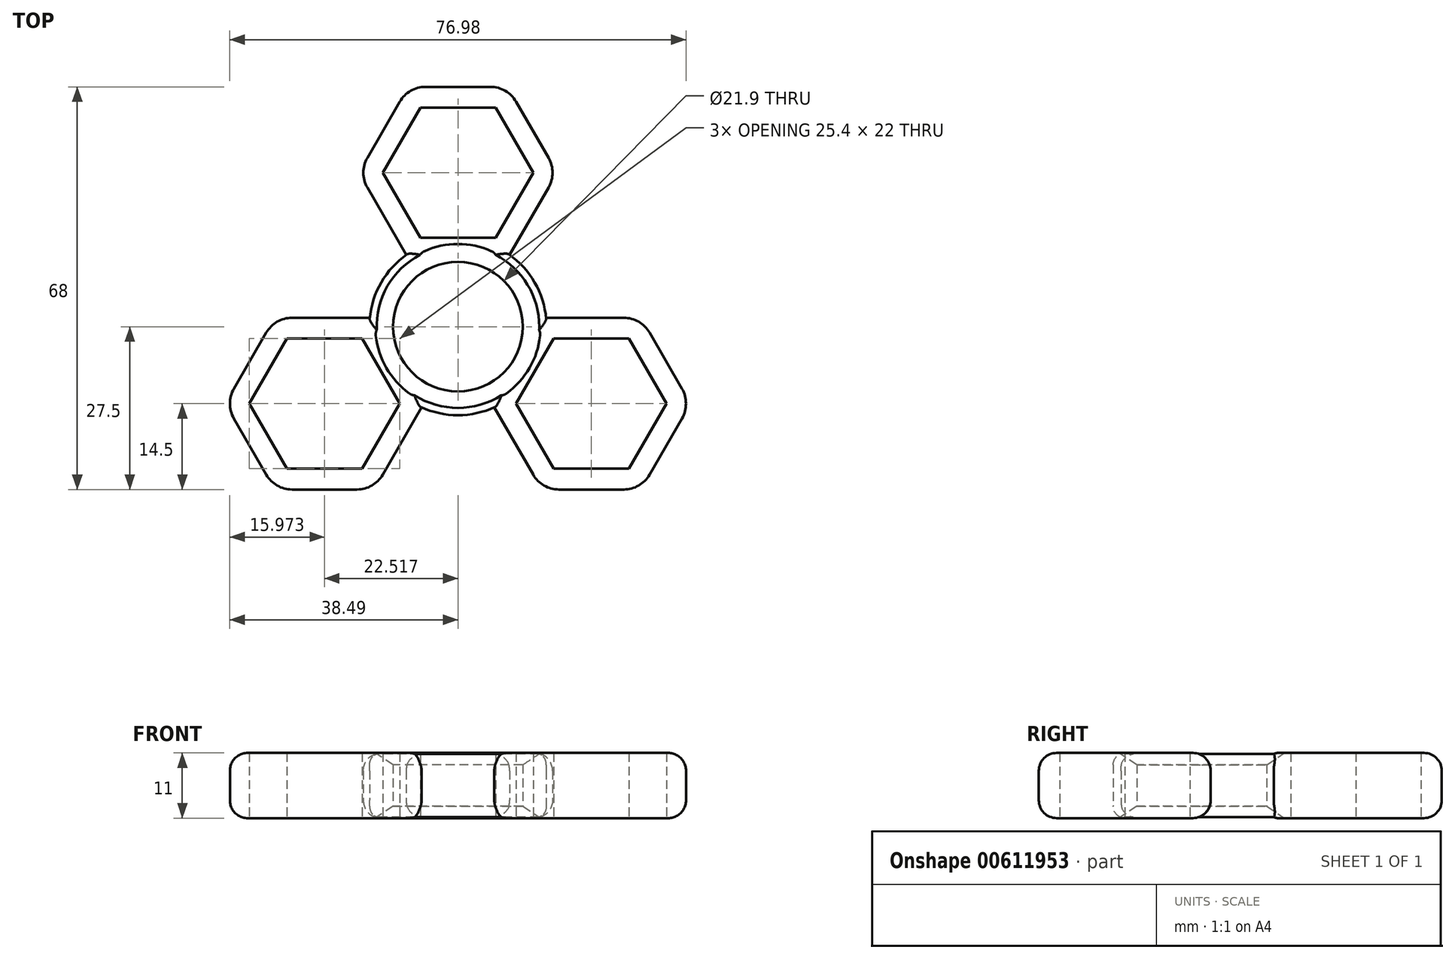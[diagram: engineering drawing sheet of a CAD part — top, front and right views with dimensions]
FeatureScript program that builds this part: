
annotation { "Feature Type Name" : "Feature", "Feature Type Description" : "" }
export const myFeature = defineFeature(function(context is Context, id is Id, definition is map)
    precondition{}
    {
        {
            var Q0;
            Q0=qCreatedBy(makeId("Top.planeOp"),FACE);
            var sketch = newSketch(context, id + "F0", { "sketchPlane" : qUnion([Q0])});
            skCircle(sketch, "E0", {"center": v(0, 0) * mm, "radius": 10.95 * mm});
            skCircle(sketch, "E1.cCircle", {"center": v(0, 0) * mm, "radius": 13 * mm, "construction": true});
            skLineSegment(sketch, "E1.0", {"start": v(0, 26) * mm, "end": v(22.52, -13) * mm, "construction": true});
            skLineSegment(sketch, "E1.1", {"start": v(22.52, -13) * mm, "end": v(-22.52, -13) * mm, "construction": true});
            skLineSegment(sketch, "E1.2", {"start": v(-22.52, -13) * mm, "end": v(0, 26) * mm, "construction": true});
            skPoint(sketch, "E1.0.midPoint", {"position": v(11.26, 6.5) * mm});
            skLineSegment(sketch, "E2", {"start": v(0, 0) * mm, "end": v(-22.52, -13) * mm, "construction": true});
            skLineSegment(sketch, "E3", {"start": v(0, 0) * mm, "end": v(22.52, -13) * mm, "construction": true});
            skLineSegment(sketch, "E4", {"start": v(0, 0) * mm, "end": v(0, 26) * mm, "construction": true});
            skCircle(sketch, "E5.cCircle", {"center": v(0, 26) * mm, "radius": 11 * mm, "construction": true});
            skLineSegment(sketch, "E5.0", {"start": v(-6.35, 37) * mm, "end": v(6.35, 37) * mm});
            skLineSegment(sketch, "E5.1", {"start": v(6.35, 37) * mm, "end": v(12.7, 26) * mm});
            skLineSegment(sketch, "E5.2", {"start": v(12.7, 26) * mm, "end": v(6.35, 15) * mm});
            skLineSegment(sketch, "E5.3", {"start": v(6.35, 15) * mm, "end": v(-6.35, 15) * mm});
            skLineSegment(sketch, "E5.4", {"start": v(-6.35, 15) * mm, "end": v(-12.7, 26) * mm});
            skLineSegment(sketch, "E5.5", {"start": v(-12.7, 26) * mm, "end": v(-6.35, 37) * mm});
            skPoint(sketch, "E5.0.midPoint", {"position": v(0, 37) * mm});
            skCircle(sketch, "E6.cCircle", {"center": v(22.52, -13) * mm, "radius": 11 * mm, "construction": true});
            skLineSegment(sketch, "E6.0", {"start": v(35.22, -13) * mm, "end": v(28.87, -24) * mm});
            skLineSegment(sketch, "E6.1", {"start": v(28.87, -24) * mm, "end": v(16.17, -24) * mm});
            skLineSegment(sketch, "E6.2", {"start": v(16.17, -24) * mm, "end": v(9.81, -13) * mm});
            skLineSegment(sketch, "E6.3", {"start": v(9.81, -13) * mm, "end": v(16.17, -2) * mm});
            skLineSegment(sketch, "E6.4", {"start": v(16.17, -2) * mm, "end": v(28.87, -2) * mm});
            skLineSegment(sketch, "E6.5", {"start": v(28.87, -2) * mm, "end": v(35.22, -13) * mm});
            skPoint(sketch, "E6.0.midPoint", {"position": v(32.04, -18.5) * mm});
            skCircle(sketch, "E7.cCircle", {"center": v(-22.52, -13) * mm, "radius": 11 * mm, "construction": true});
            skLineSegment(sketch, "E7.0", {"start": v(-28.87, -24) * mm, "end": v(-35.22, -13) * mm});
            skLineSegment(sketch, "E7.1", {"start": v(-35.22, -13) * mm, "end": v(-28.87, -2) * mm});
            skLineSegment(sketch, "E7.2", {"start": v(-28.87, -2) * mm, "end": v(-16.17, -2) * mm});
            skLineSegment(sketch, "E7.3", {"start": v(-16.17, -2) * mm, "end": v(-9.81, -13) * mm});
            skLineSegment(sketch, "E7.4", {"start": v(-9.81, -13) * mm, "end": v(-16.17, -24) * mm});
            skLineSegment(sketch, "E7.5", {"start": v(-16.17, -24) * mm, "end": v(-28.87, -24) * mm});
            skPoint(sketch, "E7.0.midPoint", {"position": v(-32.04, -18.5) * mm});
            skLineSegment(sketch, "E8.0", {"start": v(-16.74, 26) * mm, "end": v(-8.37, 40.5) * mm});
            skLineSegment(sketch, "E8.1", {"start": v(8.37, 40.5) * mm, "end": v(16.74, 26) * mm});
            skLineSegment(sketch, "E8.2", {"start": v(16.74, 26) * mm, "end": v(8.37, 11.5) * mm});
            skLineSegment(sketch, "E8.3", {"start": v(-8.37, 40.5) * mm, "end": v(8.37, 40.5) * mm});
            skLineSegment(sketch, "E8.4", {"start": v(8.37, 11.5) * mm, "end": v(-8.37, 11.5) * mm});
            skLineSegment(sketch, "E8.5", {"start": v(-8.37, 11.5) * mm, "end": v(-16.74, 26) * mm});
            skLineSegment(sketch, "E9.0", {"start": v(5.77, -13) * mm, "end": v(14.15, 1.5) * mm});
            skLineSegment(sketch, "E9.1", {"start": v(30.89, 1.5) * mm, "end": v(39.26, -13) * mm});
            skLineSegment(sketch, "E9.2", {"start": v(39.26, -13) * mm, "end": v(30.89, -27.5) * mm});
            skLineSegment(sketch, "E9.3", {"start": v(14.15, 1.5) * mm, "end": v(30.89, 1.5) * mm});
            skLineSegment(sketch, "E9.4", {"start": v(30.89, -27.5) * mm, "end": v(14.15, -27.5) * mm});
            skLineSegment(sketch, "E9.5", {"start": v(14.15, -27.5) * mm, "end": v(5.77, -13) * mm});
            skLineSegment(sketch, "E10.0", {"start": v(-39.26, -13) * mm, "end": v(-30.89, 1.5) * mm});
            skLineSegment(sketch, "E10.1", {"start": v(-14.15, 1.5) * mm, "end": v(-5.77, -13) * mm});
            skLineSegment(sketch, "E10.2", {"start": v(-5.77, -13) * mm, "end": v(-14.15, -27.5) * mm});
            skLineSegment(sketch, "E10.3", {"start": v(-30.89, 1.5) * mm, "end": v(-14.15, 1.5) * mm});
            skLineSegment(sketch, "E10.4", {"start": v(-14.15, -27.5) * mm, "end": v(-30.89, -27.5) * mm});
            skLineSegment(sketch, "E10.5", {"start": v(-30.89, -27.5) * mm, "end": v(-39.26, -13) * mm});
            skCircle(sketch, "E11.0", {"center": v(0, 0) * mm, "radius": 14.95 * mm});
            skSolve(sketch);
        }
        {
            var Q0;
            Q0=qSketchRegion(id+"F0",true);
            extrude(context, id + "F1", {"entities" : qUnion([Q0]), "depth" : 11 * mm, "offsetDistance" : 25 * mm});
        }
        {
            var Q0;
            Q0=makeQuery(id+"F1.opExtrude","SWEPT_EDGE",EDGE,{"disambiguationData":[OSD([sQuery(id+"F0.wireOp",EDGE,"E9.4"),sQuery(id+"F0.wireOp",EDGE,"E9.5")])]});
            var Q1;
            Q1=makeQuery(id+"F1.opExtrude","SWEPT_EDGE",EDGE,{"disambiguationData":[OSD([sQuery(id+"F0.wireOp",EDGE,"E9.2"),sQuery(id+"F0.wireOp",EDGE,"E9.4")])]});
            var Q2;
            Q2=makeQuery(id+"F1.opExtrude","SWEPT_EDGE",EDGE,{"disambiguationData":[OSD([sQuery(id+"F0.wireOp",EDGE,"E9.1"),sQuery(id+"F0.wireOp",EDGE,"E9.2")])]});
            var Q3;
            Q3=makeQuery(id+"F1.opExtrude","SWEPT_EDGE",EDGE,{"disambiguationData":[OSD([sQuery(id+"F0.wireOp",EDGE,"E9.1"),sQuery(id+"F0.wireOp",EDGE,"E9.3")])]});
            var Q4;
            Q4=makeQuery(id+"F1.opExtrude","SWEPT_EDGE",EDGE,{"disambiguationData":[OSD([sQuery(id+"F0.wireOp",EDGE,"E8.1"),sQuery(id+"F0.wireOp",EDGE,"E8.2")])]});
            var Q5;
            Q5=makeQuery(id+"F1.opExtrude","SWEPT_EDGE",EDGE,{"disambiguationData":[OSD([sQuery(id+"F0.wireOp",EDGE,"E8.1"),sQuery(id+"F0.wireOp",EDGE,"E8.3")])]});
            var Q6;
            Q6=makeQuery(id+"F1.opExtrude","SWEPT_EDGE",EDGE,{"disambiguationData":[OSD([sQuery(id+"F0.wireOp",EDGE,"E8.0"),sQuery(id+"F0.wireOp",EDGE,"E8.3")])]});
            var Q7;
            Q7=makeQuery(id+"F1.opExtrude","SWEPT_EDGE",EDGE,{"disambiguationData":[OSD([sQuery(id+"F0.wireOp",EDGE,"E8.0"),sQuery(id+"F0.wireOp",EDGE,"E8.5")])]});
            var Q8;
            Q8=makeQuery(id+"F1.opExtrude","SWEPT_EDGE",EDGE,{"disambiguationData":[OSD([sQuery(id+"F0.wireOp",EDGE,"E10.0"),sQuery(id+"F0.wireOp",EDGE,"E10.3")])]});
            var Q9;
            Q9=makeQuery(id+"F1.opExtrude","SWEPT_EDGE",EDGE,{"disambiguationData":[OSD([sQuery(id+"F0.wireOp",EDGE,"E10.0"),sQuery(id+"F0.wireOp",EDGE,"E10.5")])]});
            var Q10;
            Q10=makeQuery(id+"F1.opExtrude","SWEPT_EDGE",EDGE,{"disambiguationData":[OSD([sQuery(id+"F0.wireOp",EDGE,"E10.4"),sQuery(id+"F0.wireOp",EDGE,"E10.5")])]});
            var Q11;
            Q11=makeQuery(id+"F1.opExtrude","SWEPT_EDGE",EDGE,{"disambiguationData":[OSD([sQuery(id+"F0.wireOp",EDGE,"E10.2"),sQuery(id+"F0.wireOp",EDGE,"E10.4")])]});
            fillet(context, id + "F2", {"entities" : qUnion([Q0, Q1, Q2, Q3, Q4, Q5, Q6, Q7, Q8, Q9, Q10, Q11]), "radius" : 5 * mm, "tangentPropagation" : true, "allowEdgeOverflow" : false});
        }
        {
            var Q0;
            Q0=makeQuery(id+"F1.opExtrude","CAP_EDGE",EDGE,{"disambiguationData":[OSD([sQuery(id+"F0.wireOp",EDGE,"E0")])],"isStart":true});
            var Q1;
            Q1=makeQuery(id+"F1.opExtrude","CAP_EDGE",EDGE,{"disambiguationData":[OSD([sQuery(id+"F0.wireOp",EDGE,"E0")])],"isStart":false});
            chamfer(context, id + "F3", {"entities" : qUnion([Q0, Q1]), "chamferType" : ChamferType.TWO_OFFSETS, "width1" : 3 * mm, "oppositeDirection" : false, "width2" : 2 * mm, "tangentPropagation" : true});
        }
        {
            var Q0;
            Q0=makeQuery(id+"F1.opExtrude","CAP_EDGE",EDGE,{"disambiguationData":[OSD([sQuery(id+"F0.wireOp",EDGE,"E10.4")])],"isStart":false});
            var Q1;
            Q1=makeQuery(id+"F1.opExtrude","CAP_EDGE",EDGE,{"disambiguationData":[OSD([sQuery(id+"F0.wireOp",EDGE,"E9.5")])],"isStart":false});
            var Q2;
            Q2=makeQuery(id+"F1.opExtrude","CAP_EDGE",EDGE,{"disambiguationData":[OSD([sQuery(id+"F0.wireOp",EDGE,"E8.2")])],"isStart":false});
            var Q3;
            Q3=makeQuery(id+"F1.opExtrude","CAP_EDGE",EDGE,{"disambiguationData":[OSD([sQuery(id+"F0.wireOp",EDGE,"E8.2")])],"isStart":true});
            var Q4;
            Q4=makeQuery(id+"F1.opExtrude","CAP_EDGE",EDGE,{"disambiguationData":[OSD([sQuery(id+"F0.wireOp",EDGE,"E9.3")])],"isStart":true});
            var Q5;
            Q5=makeQuery(id+"F1.opExtrude","CAP_EDGE",EDGE,{"disambiguationData":[OSD([sQuery(id+"F0.wireOp",EDGE,"E10.2")])],"isStart":true});
            fillet(context, id + "F4", {"entities" : qUnion([Q0, Q1, Q2, Q3, Q4, Q5]), "radius" : 3 * mm, "tangentPropagation" : true, "allowEdgeOverflow" : false});
        }
        {
            var Q0;
            {var subQ0=sQuery(id+"F0.wireOp",EDGE,"E11.0");Q0=makeQuery(id+"F1.opExtrude","CAP_EDGE",EDGE,{"disambiguationData":[OSD([subQ0]),TDD([makeQuery(id+"F0.imprint","IMPRINT",EDGE,{"disambiguationData":[TD([[makeQuery(id+"F0.imprint","INTERSECT",VERTEX,{"derivedFrom":[sQuery(id+"F0.wireOp",EDGE,"E9.5"),subQ0]}),1.0]])],"derivedFrom":subQ0})])],"isStart":false});}
            var Q1;
            {var subQ0=sQuery(id+"F0.wireOp",EDGE,"E11.0");Q1=makeQuery(id+"F1.opExtrude","CAP_EDGE",EDGE,{"disambiguationData":[OSD([subQ0]),TDD([makeQuery(id+"F0.imprint","IMPRINT",EDGE,{"disambiguationData":[TD([[makeQuery(id+"F0.imprint","INTERSECT",VERTEX,{"derivedFrom":[sQuery(id+"F0.wireOp",EDGE,"E8.2"),subQ0]}),1.0]])],"derivedFrom":subQ0})])],"isStart":false});}
            var Q2;
            {var subQ0=sQuery(id+"F0.wireOp",EDGE,"E11.0");Q2=makeQuery(id+"F1.opExtrude","CAP_EDGE",EDGE,{"disambiguationData":[OSD([subQ0]),TDD([makeQuery(id+"F0.imprint","IMPRINT",EDGE,{"disambiguationData":[TD([[makeQuery(id+"F0.imprint","INTERSECT",VERTEX,{"derivedFrom":[sQuery(id+"F0.wireOp",EDGE,"E8.5"),subQ0]}),-1.0]])],"derivedFrom":subQ0})])],"isStart":false});}
            var Q3;
            {var subQ0=sQuery(id+"F0.wireOp",EDGE,"E11.0");Q3=makeQuery(id+"F1.opExtrude","CAP_EDGE",EDGE,{"disambiguationData":[OSD([subQ0]),TDD([makeQuery(id+"F0.imprint","IMPRINT",EDGE,{"disambiguationData":[TD([[makeQuery(id+"F0.imprint","INTERSECT",VERTEX,{"derivedFrom":[sQuery(id+"F0.wireOp",EDGE,"E8.2"),subQ0]}),1.0]])],"derivedFrom":subQ0})])],"isStart":true});}
            var Q4;
            {var subQ0=sQuery(id+"F0.wireOp",EDGE,"E11.0");Q4=makeQuery(id+"F1.opExtrude","CAP_EDGE",EDGE,{"disambiguationData":[OSD([subQ0]),TDD([makeQuery(id+"F0.imprint","IMPRINT",EDGE,{"disambiguationData":[TD([[makeQuery(id+"F0.imprint","INTERSECT",VERTEX,{"derivedFrom":[sQuery(id+"F0.wireOp",EDGE,"E9.5"),subQ0]}),1.0]])],"derivedFrom":subQ0})])],"isStart":true});}
            var Q5;
            {var subQ0=sQuery(id+"F0.wireOp",EDGE,"E11.0");Q5=makeQuery(id+"F1.opExtrude","CAP_EDGE",EDGE,{"disambiguationData":[OSD([subQ0]),TDD([makeQuery(id+"F0.imprint","IMPRINT",EDGE,{"disambiguationData":[TD([[makeQuery(id+"F0.imprint","INTERSECT",VERTEX,{"derivedFrom":[sQuery(id+"F0.wireOp",EDGE,"E8.5"),subQ0]}),-1.0]])],"derivedFrom":subQ0})])],"isStart":true});}
            fillet(context, id + "F5", {"entities" : qUnion([Q0, Q1, Q2, Q3, Q4, Q5]), "radius" : 2 * mm, "tangentPropagation" : true, "allowEdgeOverflow" : false});
        }
    });
